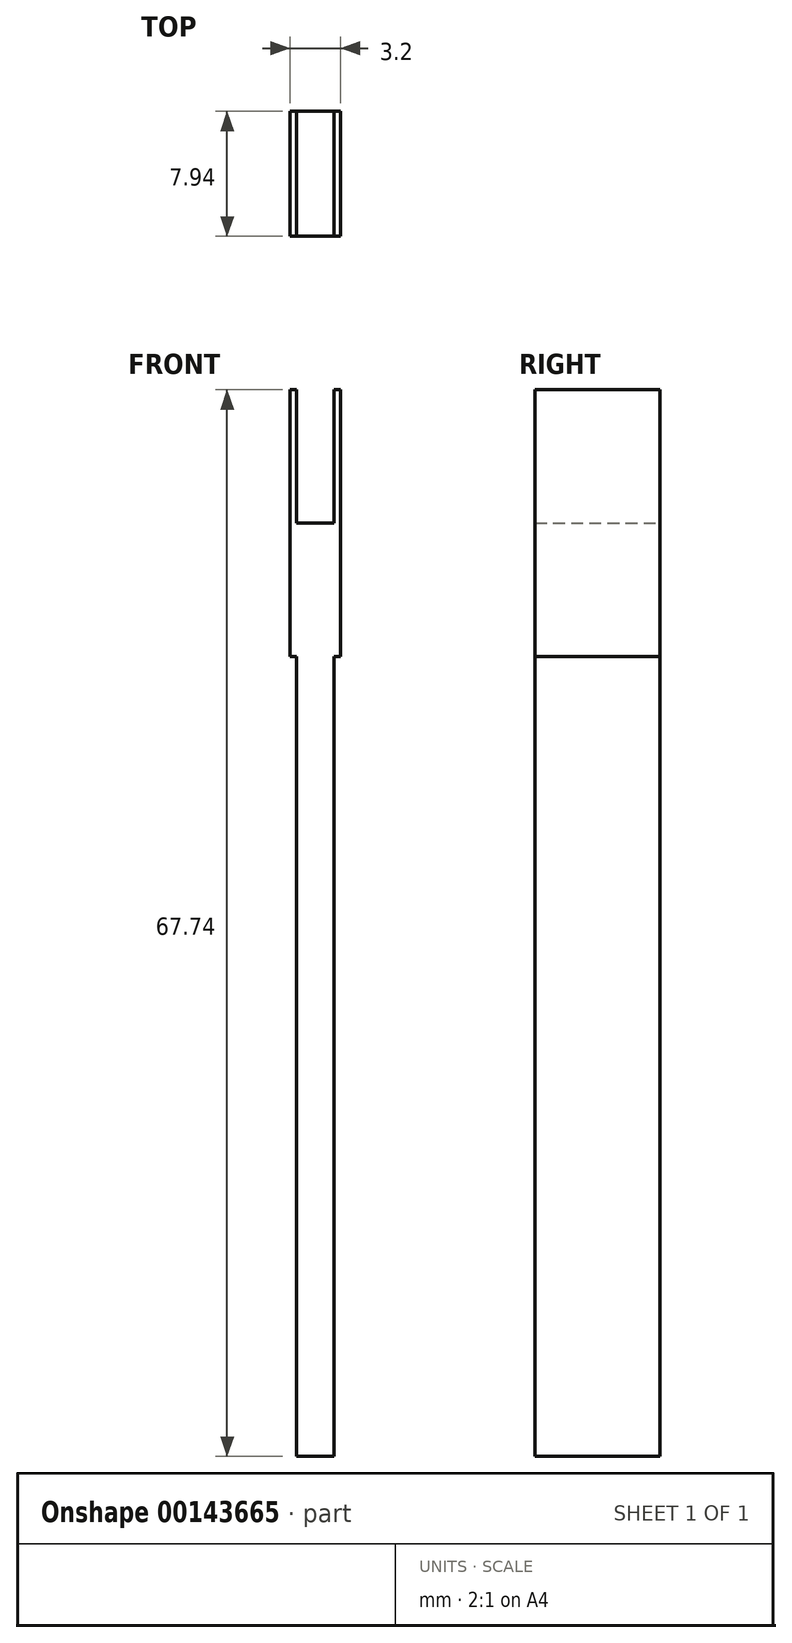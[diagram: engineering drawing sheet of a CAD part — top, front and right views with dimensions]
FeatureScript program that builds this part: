
annotation { "Feature Type Name" : "Feature", "Feature Type Description" : "" }
export const myFeature = defineFeature(function(context is Context, id is Id, definition is map)
    precondition{}
    {
        {
            var Q0;
            Q0=qCreatedBy(makeId("Front.planeOp"),FACE);
            var sketch = newSketch(context, id + "F0", { "sketchPlane" : qUnion([Q0])});
            skLineSegment(sketch, "E0", {"start": v(-42.33, 33.5) * mm, "end": v(-42.33, -8.41) * mm, "construction": true});
            skLineSegment(sketch, "E1.bottom", {"start": v(-45.73, 34.94) * mm, "end": v(-43.35, 34.94) * mm});
            skLineSegment(sketch, "E1.top", {"start": v(-45.73, -24.33) * mm, "end": v(-43.35, -24.33) * mm});
            skLineSegment(sketch, "E1.left", {"start": v(-45.73, 34.94) * mm, "end": v(-45.73, -24.33) * mm});
            skLineSegment(sketch, "E1.right", {"start": v(-43.35, 34.94) * mm, "end": v(-43.35, -24.33) * mm});
            skLineSegment(sketch, "E2.bottom", {"start": v(-42.94, 26.47) * mm, "end": v(-46.14, 26.47) * mm});
            skLineSegment(sketch, "E2.top", {"start": v(-42.94, 43.4) * mm, "end": v(-43.35, 43.4) * mm});
            skLineSegment(sketch, "E2.left", {"start": v(-42.94, 26.47) * mm, "end": v(-42.94, 43.4) * mm});
            skLineSegment(sketch, "E2.right", {"start": v(-46.14, 26.47) * mm, "end": v(-46.14, 43.4) * mm});
            skLineSegment(sketch, "E3", {"start": v(-45.73, 43.4) * mm, "end": v(-45.73, 34.94) * mm});
            skLineSegment(sketch, "E4", {"start": v(-43.35, 43.4) * mm, "end": v(-43.35, 26.47) * mm});
            skLineSegment(sketch, "E5.trimOffspring", {"start": v(-45.73, 43.4) * mm, "end": v(-46.14, 43.4) * mm});
            skSolve(sketch);
        }
        {
            var Q0;
            {var subQ1=sQuery(id+"F0.wireOp",EDGE,"E2.right");Q0=makeQuery(id+"F0.imprint","IMPRINT",FACE,{"disambiguationData":[TD([[makeQuery(id+"F0.imprint","IMPRINT",EDGE,{"derivedFrom":subQ1}),-1.0]])]});}
            var Q1;
            {var subQ2=sQuery(id+"F0.wireOp",EDGE,"E2.top");Q1=makeQuery(id+"F0.imprint","IMPRINT",FACE,{"disambiguationData":[TD([[makeQuery(id+"F0.imprint","IMPRINT",EDGE,{"derivedFrom":subQ2}),1.0]])]});}
            var Q2;
            {var subQ0=sQuery(id+"F0.wireOp",EDGE,"E1.top");Q2=makeQuery(id+"F0.imprint","IMPRINT",FACE,{"disambiguationData":[TD([[makeQuery(id+"F0.imprint","IMPRINT",EDGE,{"derivedFrom":subQ0}),1.0]])]});}
            var Q3;
            {var subQ0=sQuery(id+"F0.wireOp",EDGE,"E1.bottom");Q3=makeQuery(id+"F0.imprint","IMPRINT",FACE,{"disambiguationData":[TD([[makeQuery(id+"F0.imprint","IMPRINT",EDGE,{"derivedFrom":subQ0}),-1.0]])]});}
            extrude(context, id + "F1", {"entities" : qUnion([Q0, Q1, Q2, Q3]), "depth" : 7.94 * mm});
        }
    });
